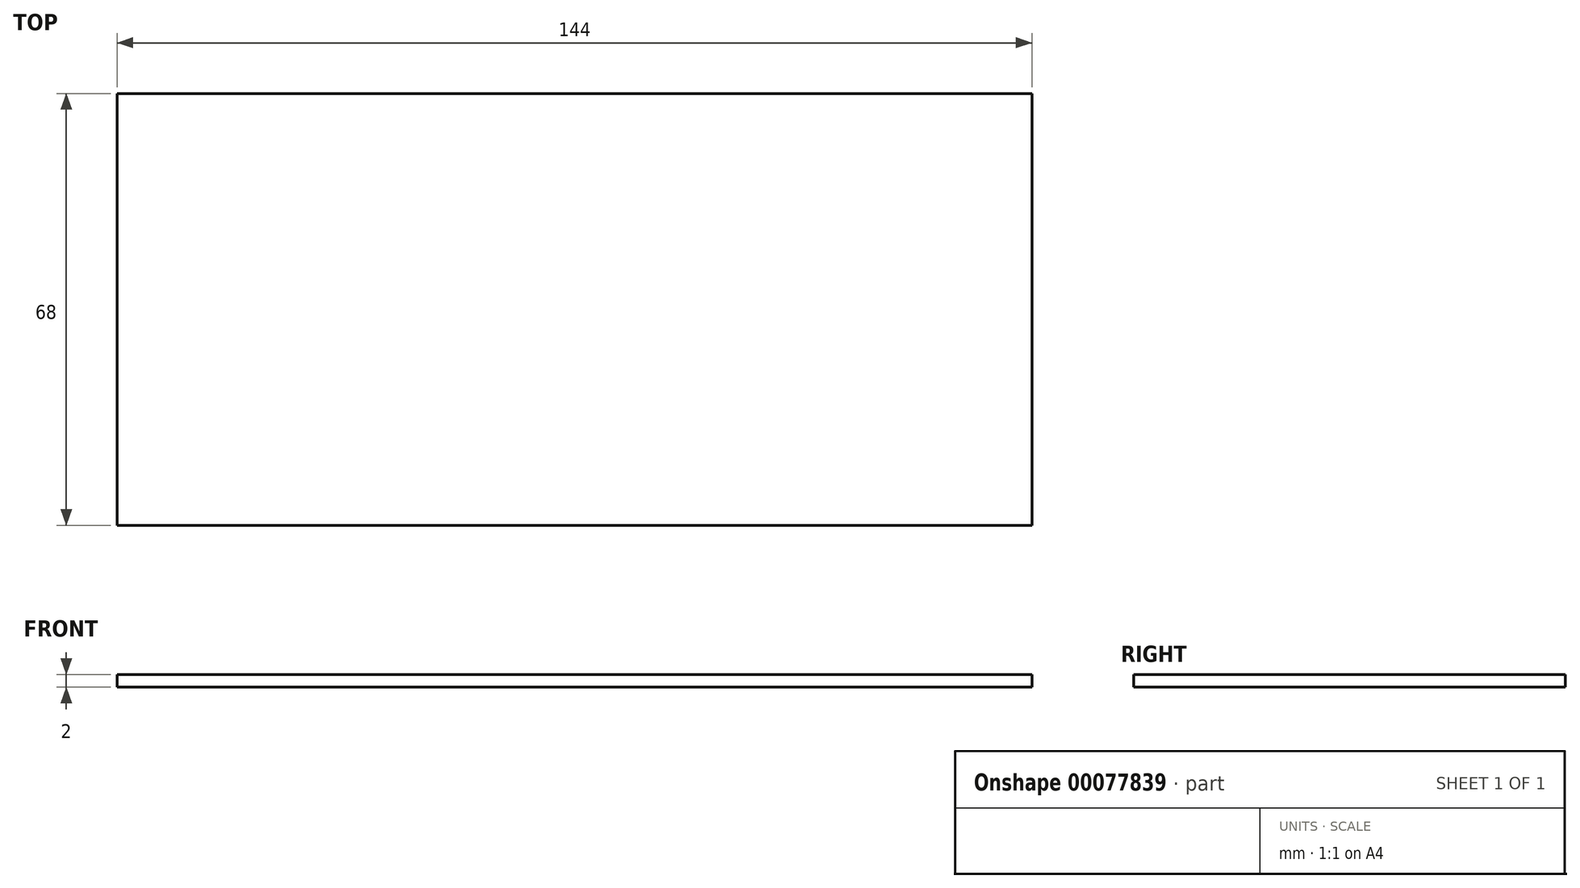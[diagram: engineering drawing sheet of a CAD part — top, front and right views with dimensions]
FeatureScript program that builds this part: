
annotation { "Feature Type Name" : "Feature", "Feature Type Description" : "" }
export const myFeature = defineFeature(function(context is Context, id is Id, definition is map)
    precondition{}
    {
        {
            var Q0;
            Q0=qCreatedBy(makeId("Top.planeOp"),FACE);
            var sketch = newSketch(context, id + "F0", { "sketchPlane" : qUnion([Q0])});
            skLineSegment(sketch, "E0.bottom", {"start": v(-72, 34) * mm, "end": v(72, 34) * mm});
            skLineSegment(sketch, "E0.top", {"start": v(-72, -34) * mm, "end": v(72, -34) * mm});
            skLineSegment(sketch, "E0.left", {"start": v(-72, 34) * mm, "end": v(-72, -34) * mm});
            skLineSegment(sketch, "E0.right", {"start": v(72, 34) * mm, "end": v(72, -34) * mm});
            skSolve(sketch);
        }
        {
            var Q0;
            Q0=makeQuery(id+"F0.imprint","IMPRINT",FACE,{"disambiguationData":[TD([[makeQuery(id+"F0.imprint","IMPRINT",EDGE,{"derivedFrom":sQuery(id+"F0.wireOp",EDGE,"E0.bottom")}),-1.0]])]});
            extrude(context, id + "F1", {"entities" : qUnion([Q0]), "depth" : 2 * mm});
        }
    });
